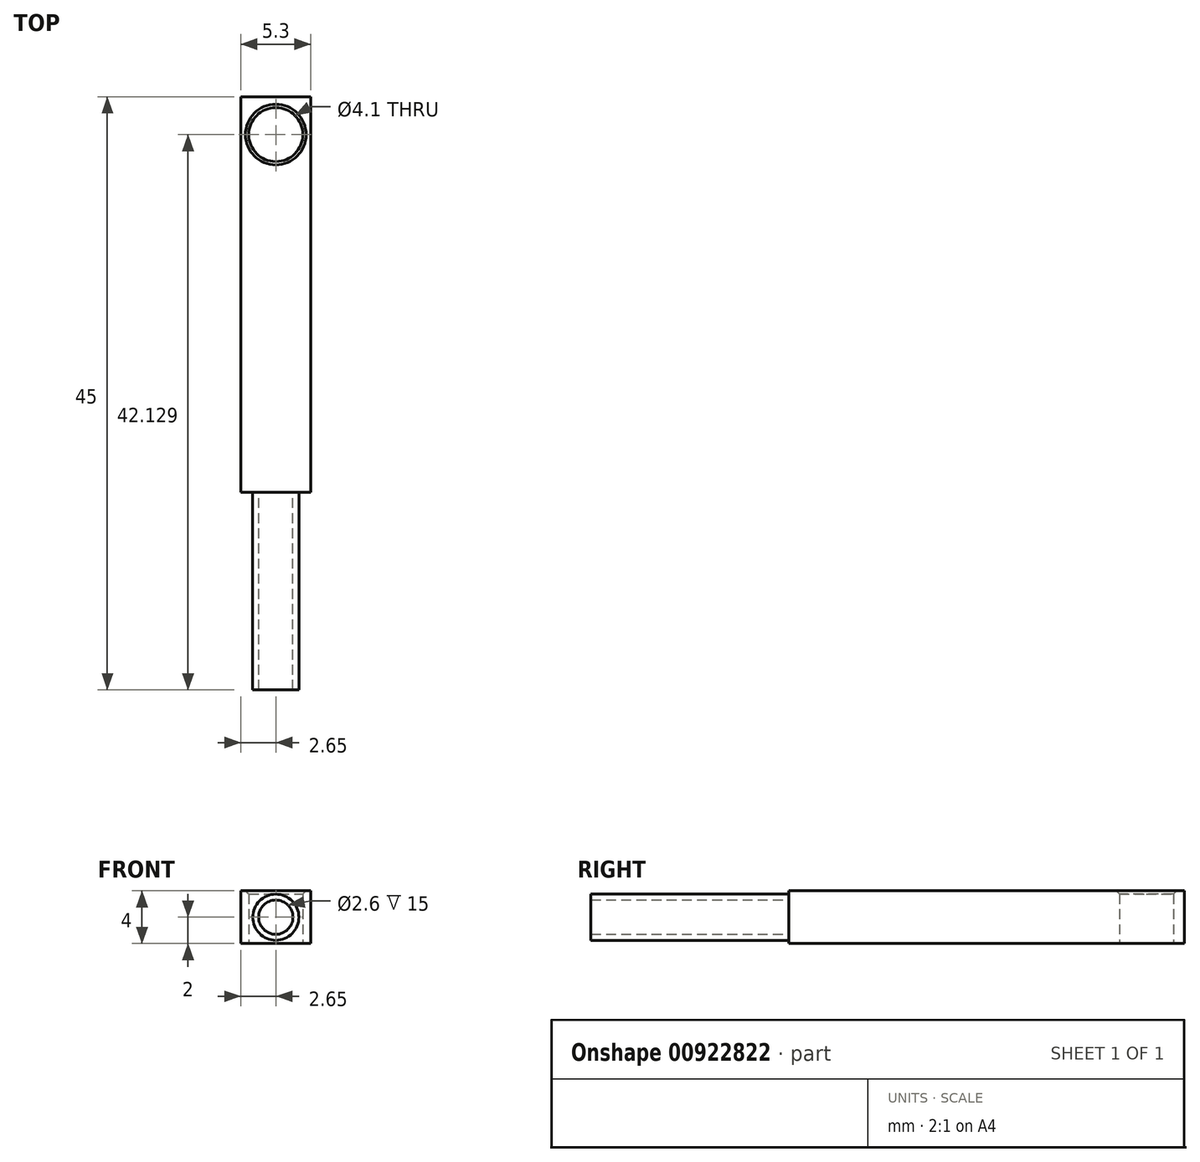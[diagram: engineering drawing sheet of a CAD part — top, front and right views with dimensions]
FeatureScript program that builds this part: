
annotation { "Feature Type Name" : "Feature", "Feature Type Description" : "" }
export const myFeature = defineFeature(function(context is Context, id is Id, definition is map)
    precondition{}
    {
        {
            var Q0;
            Q0=qCreatedBy(makeId("Front.planeOp"),FACE);
            var sketch = newSketch(context, id + "F0", { "sketchPlane" : qUnion([Q0])});
            skLineSegment(sketch, "E0.bottom", {"start": v(-2.65, -2) * mm, "end": v(2.65, -2) * mm});
            skLineSegment(sketch, "E0.top", {"start": v(-2.65, 2) * mm, "end": v(2.65, 2) * mm});
            skLineSegment(sketch, "E0.left", {"start": v(-2.65, -2) * mm, "end": v(-2.65, 2) * mm});
            skLineSegment(sketch, "E0.right", {"start": v(2.65, -2) * mm, "end": v(2.65, 2) * mm});
            skPoint(sketch, "E0.middle", {"position": v(0, 0) * mm});
            skSolve(sketch);
        }
        {
            var Q0;
            Q0 = qSketchRegion(id + "F0", true);
            extrude(context, id + "F1", {"entities" : qUnion([Q0]), "oppositeDirection" : true, "depth" : 30 * mm, "offsetDistance" : 25 * mm});
        }
        {
            var Q0;
            Q0=makeQuery(id+"F1.opExtrude","CAP_FACE",FACE,{"disambiguationData":[OSD([sQuery(id+"F0.wireOp",EDGE,"E0.bottom"),sQuery(id+"F0.wireOp",EDGE,"E0.top"),sQuery(id+"F0.wireOp",EDGE,"E0.left"),sQuery(id+"F0.wireOp",EDGE,"E0.right")])],"isStart":true});
            var sketch = newSketch(context, id + "F2", { "sketchPlane" : qUnion([Q0])});
            skCircle(sketch, "E1", {"center": v(0, 0) * mm, "radius": 1.75 * mm});
            skCircle(sketch, "E2", {"center": v(0, 0) * mm, "radius": 1.3 * mm});
            skSolve(sketch);
        }
        {
            var Q0;
            Q0 = qSketchRegion(id + "F2", true);
            extrude(context, id + "F3", {"entities" : qUnion([Q0]), "operationType" : NewBodyOperationType.ADD, "depth" : 15 * mm, "offsetDistance" : 25 * mm});
        }
        {
            var Q0;
            Q0=makeQuery(id+"F3.boolean.opBoolean","SPLIT",FACE,{"disambiguationData":[TD([makeQuery(id+"F3.opExtrude","SWEPT_FACE",FACE,{"disambiguationData":[OSD([sQuery(id+"F2.wireOp",EDGE,"E2")])]})])],"derivedFrom":makeQuery(id+"F1.opExtrude","CAP_FACE",FACE,{"disambiguationData":[OSD([sQuery(id+"F0.wireOp",EDGE,"E0.bottom"),sQuery(id+"F0.wireOp",EDGE,"E0.top"),sQuery(id+"F0.wireOp",EDGE,"E0.left"),sQuery(id+"F0.wireOp",EDGE,"E0.right")])],"isStart":true})});
            var sketch = newSketch(context, id + "F4", { "sketchPlane" : qUnion([Q0])});
            skSolve(sketch);
        }
        {
            var Q0;
            Q0=makeQuery(id+"F4.imprint","IMPRINT",FACE,{"disambiguationData":[TD([[makeQuery(id+"F4.imprint","IMPRINT",EDGE,{"derivedFrom":makeQuery(id+"F3.opExtrude","CAP_EDGE",EDGE,{"disambiguationData":[OSD([sQuery(id+"F2.wireOp",EDGE,"E2")])],"isStart":true})}),1.0]])]});
            extrude(context, id + "F5", {"entities" : qUnion([Q0]), "operationType" : NewBodyOperationType.ADD, "oppositeDirection" : true, "depth" : 25.8 * mm, "offsetDistance" : 25 * mm});
        }
        {
            var Q0;
            Q0=makeQuery(id+"F1.opExtrude","SWEPT_FACE",FACE,{"disambiguationData":[OSD([sQuery(id+"F0.wireOp",EDGE,"E0.bottom")])]});
            var sketch = newSketch(context, id + "F6", { "sketchPlane" : qUnion([Q0])});
            skLineSegment(sketch, "E3", {"start": v(0, -44.65) * mm, "end": v(0, 23.78) * mm, "construction": true});
            skCircle(sketch, "E4", {"center": v(0, -27.13) * mm, "radius": 2.05 * mm});
            skSolve(sketch);
        }
        {
            var Q0;
            Q0 = qSketchRegion(id + "F6", true);
            extrude(context, id + "F7", {"entities" : qUnion([Q0]), "operationType" : NewBodyOperationType.REMOVE, "oppositeDirection" : true, "depth" : 5 * mm, "offsetDistance" : 25 * mm});
        }
        {
            var Q0;
            Q0=makeQuery(id+"F7.boolean.opBoolean","COPY",EDGE,{"derivedFrom":makeQuery(id+"F7.opExtrude","CAP_EDGE",EDGE,{"disambiguationData":[OSD([sQuery(id+"F6.wireOp",EDGE,"E4")])],"isStart":true})});
            var Q1;
            Q1=makeQuery(id+"F7.boolean.opBoolean","INTERSECT",EDGE,{"derivedFrom":[makeQuery(id+"F1.opExtrude","SWEPT_FACE",FACE,{"disambiguationData":[OSD([sQuery(id+"F0.wireOp",EDGE,"E0.top")])]}),makeQuery(id+"F7.opExtrude","SWEPT_FACE",FACE,{"disambiguationData":[OSD([sQuery(id+"F6.wireOp",EDGE,"E4")])]})]});
            chamfer(context, id + "F8", {"entities" : qUnion([Q0, Q1]), "width" : 0.25 * mm, "tangentPropagation" : true});
        }
    });
